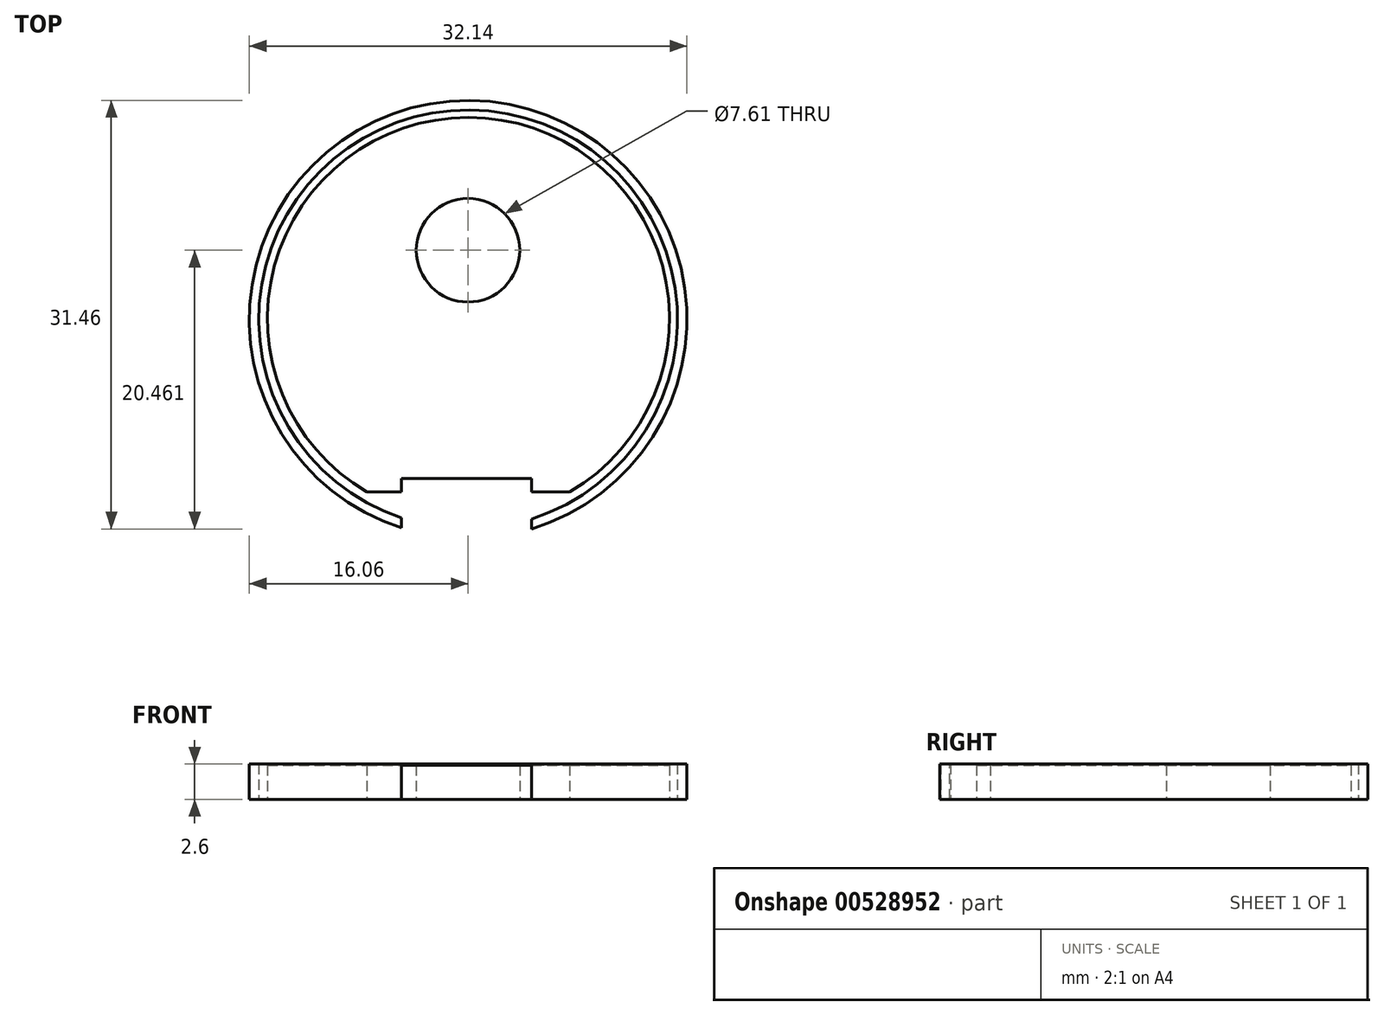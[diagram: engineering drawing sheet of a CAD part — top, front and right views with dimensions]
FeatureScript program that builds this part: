
annotation { "Feature Type Name" : "Feature", "Feature Type Description" : "" }
export const myFeature = defineFeature(function(context is Context, id is Id, definition is map)
    precondition{}
    {
        {
            var Q0;
            Q0=qCreatedBy(makeId("Top.planeOp"),FACE);
            var sketch = newSketch(context, id + "F0", { "sketchPlane" : qUnion([Q0])});
            skLineSegment(sketch, "E0", {"start": v(-30.23, 41.68) * mm, "end": v(-15.34, 41.68) * mm});
            skArc(sketch, "E1", {"start": v(-15.34, 41.68) * mm, "mid": v(-22.79, 69.17) * mm, "end": v(-30.23, 41.68) * mm});
            skLineSegment(sketch, "E2.left", {"start": v(-30.23, 41.68) * mm, "end": v(-30.23, 41.68) * mm});
            skLineSegment(sketch, "E2.right", {"start": v(-15.34, 41.68) * mm, "end": v(-15.34, 41.68) * mm});
            skLineSegment(sketch, "E3.bottom", {"start": v(-27.68, 41.68) * mm, "end": v(-18.17, 41.68) * mm});
            skLineSegment(sketch, "E3.top", {"start": v(-27.68, 2.44) * mm, "end": v(-18.17, 2.44) * mm});
            skLineSegment(sketch, "E3.left", {"start": v(-27.68, 41.68) * mm, "end": v(-27.68, 2.44) * mm});
            skLineSegment(sketch, "E3.right", {"start": v(-18.17, 41.68) * mm, "end": v(-18.17, 2.44) * mm});
            skCircle(sketch, "E4", {"center": v(-22.82, 59.42) * mm, "radius": 3.8 * mm});
            skSolve(sketch);
        }
        {
            var Q0;
            Q0 = qSketchRegion(id + "F0", true);
            extrude(context, id + "F1", {"entities" : qUnion([Q0]), "depth" : 2.5 * mm, "offsetDistance" : 25.4 * mm});
        }
        {
            var Q0;
            Q0=qCreatedBy(makeId("Top.planeOp"),FACE);
            var sketch = newSketch(context, id + "F2", { "sketchPlane" : qUnion([Q0])});
            skCircle(sketch, "E5", {"center": v(-22.81, 54.35) * mm, "radius": 15.37 * mm});
            skCircle(sketch, "E6", {"center": v(-22.81, 54.35) * mm, "radius": 16.07 * mm});
            skSolve(sketch);
        }
        {
            var Q0;
            Q0 = qSketchRegion(id + "F2", true);
            extrude(context, id + "F3", {"entities" : qUnion([Q0]), "operationType" : NewBodyOperationType.ADD, "depth" : 2.6 * mm, "offsetDistance" : 25.4 * mm});
        }
        {
            var Q0;
            Q0=qCreatedBy(makeId("Front.planeOp"),FACE);
            var sketch = newSketch(context, id + "F4", { "sketchPlane" : qUnion([Q0])});
            skLineSegment(sketch, "E7.bottom", {"start": v(-27.7, 2.64) * mm, "end": v(-18.16, 2.64) * mm});
            skLineSegment(sketch, "E7.top", {"start": v(-27.7, 0) * mm, "end": v(-18.16, 0) * mm});
            skLineSegment(sketch, "E7.left", {"start": v(-27.7, 2.64) * mm, "end": v(-27.7, 0) * mm});
            skLineSegment(sketch, "E7.right", {"start": v(-18.16, 2.64) * mm, "end": v(-18.16, 0) * mm});
            skSolve(sketch);
        }
        {
            var Q0;
            Q0 = qSketchRegion(id + "F4", true);
            extrude(context, id + "F5", {"entities" : qUnion([Q0]), "operationType" : NewBodyOperationType.REMOVE, "oppositeDirection" : true, "depth" : 42.67 * mm, "offsetDistance" : 25.4 * mm});
        }
    });
